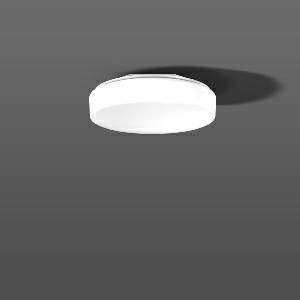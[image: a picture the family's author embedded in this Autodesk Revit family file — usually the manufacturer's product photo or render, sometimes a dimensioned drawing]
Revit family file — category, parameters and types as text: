
# Revit family: flat_polymero_kreis_672092_002_6_1_07_595a
name_source: partatom
category: Lighting Fixtures
units: mm (PartAtom-declared; Revit-internal decimal feet)

## family parameters
Cut with Voids When Loaded = No
Host = Face
Light Source = No
Part Type = Normal
Room Calculation Point = No
Round Connector Dimension = Use Diameter
Shared = No

## types (1)
- FLAT POLYMERO KREIS (1 x LED Modul 840, 1800 lm, 4000)
    Apparent Load = 15 VA
    CIE Flux Codes = 43 73 91 87 100
    Color Rendering = 80
    Color Temperature = 4000
    Default Elevation = 1800 mm  [stored 5.90551 ft]
    Description = Series: FLAT POLYMERO KREIS
Decorative round surface-mounted luminaire. For escape route illumination. Base: metal, powder-coated. Diffuser made of plastic (polycarbonate), opal, shockproof. Diffuser fastening: patented push system. Suitable for Ceiling mounting, Wall (surface). Self-contained system with automatic self-test and feedback via DALI bus, only to RZB DALI monitoring system. 
Colour: white
Diameter: 360 mm
Height: 109 mm
Weight: 1.88 kg
Operating mode: Combined NL readiness
Duration time: 3 h
Lamp: LED
Socket: without socket
Colour temperature: 4000K
Colour rendering index (CRI): 80
System power: 15 W
Rated luminous flux: 1800 lm
Luminous flux, emergency: 210 lm
System power, emergency: -
Control gear: Regulated power supply
Protection class: I
Type of protection: IP 40
    Height = 109 mm
    Lamp = 1 x LED Modul 840
    Lamp Light Flux = 1800 lm
    Lamp count = 1
    Length = 360 mm
    Lifetime = 50000 h
    Luminous efficacy = 120 lm/W
    Manufacturer = RZB
    ModVariant = No
    Model = 672092.002.6.1.07
    Mounting Place = Ceiling
    Mounting Type = Surface mounted
    Number of Poles = 1
    OnlyDefault = Yes
    Power Factor = 1
    Product Name = FLAT POLYMERO KREIS
    Product group = Surface mounted ceiling and wall luminaires
    ProductGroupID = 305
    Protection Class = Protection class I
    Protection Degree = Degree of protection
    RLX_Detail_Level = 1
    RLX_Emergency_Light_Flux = 210 lm
    RLX_Emergency_Type = 3
    RLX_Emergency_Type_DB = Yes
    RlxData = <blob elided: 52089 chars, md5=151bb449>
    Socket = socket
    Standby Power = 0 W
    System Light Flux = 1800 lm
    System Power = 15 W
    Type Comments = Product without accessories
    Type Image = 672092.002.1.jpg
    URL = http://relux.com
    VarID = ---
    Voltage = 0 V
    Weight = 0.00 kg
    Width = 0 mm  [stored 0 ft]

note: [stored X ft] marks values corroborated as IEEE doubles in the binary element streams (Revit-internal decimal feet)

## geometry (parser evidence)
native form markers: Blend x4, Sweep x14
no freeform markers — native parametric forms only
